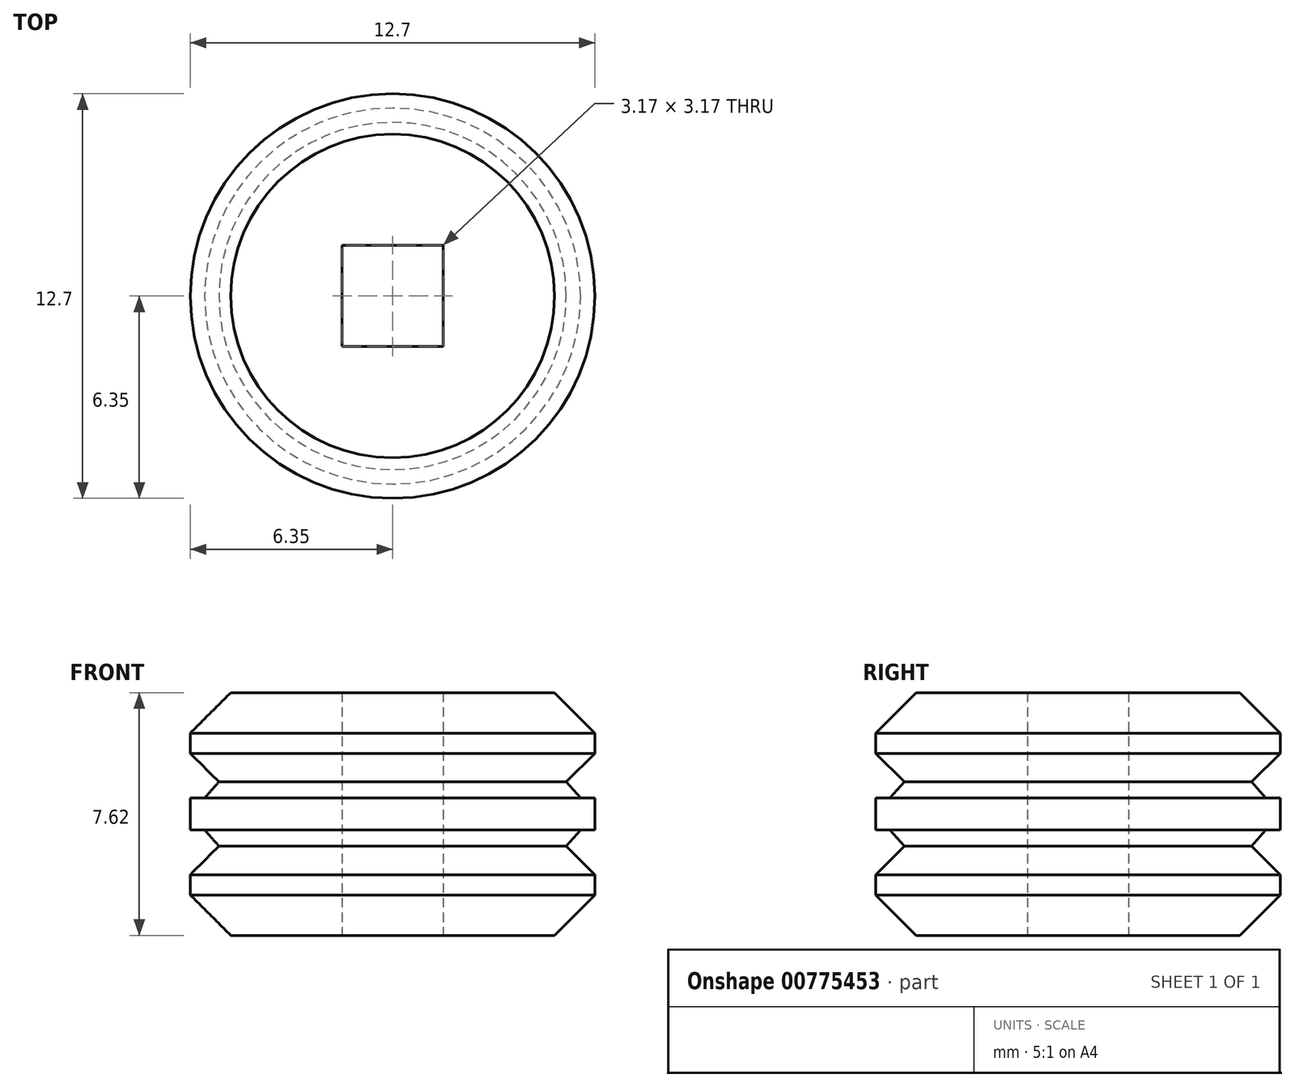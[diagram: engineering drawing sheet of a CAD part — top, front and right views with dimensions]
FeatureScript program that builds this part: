
annotation { "Feature Type Name" : "Feature", "Feature Type Description" : "" }
export const myFeature = defineFeature(function(context is Context, id is Id, definition is map)
    precondition{}
    {
        {
            var Q0;
            Q0=qCreatedBy(makeId("Front.planeOp"),FACE);
            var sketch = newSketch(context, id + "F0", { "sketchPlane" : qUnion([Q0])});
            skLineSegment(sketch, "E0.bottom", {"start": v(0, 0) * mm, "end": v(-6.35, 0) * mm});
            skLineSegment(sketch, "E0.top", {"start": v(0, 7.62) * mm, "end": v(-6.35, 7.62) * mm});
            skLineSegment(sketch, "E0.left", {"start": v(0, 0) * mm, "end": v(0, 7.62) * mm});
            skLineSegment(sketch, "E1", {"start": v(-6.35, 1.9) * mm, "end": v(-5.45, 2.8) * mm});
            skLineSegment(sketch, "E2.MirrorCS", {"start": v(-6.35, 5.72) * mm, "end": v(-5.45, 4.82) * mm});
            skLineSegment(sketch, "E3", {"start": v(-5.9, 3.3) * mm, "end": v(-6.35, 3.3) * mm});
            skLineSegment(sketch, "E4", {"start": v(-5.9, 3.3) * mm, "end": v(-5.45, 2.8) * mm});
            skLineSegment(sketch, "E5", {"start": v(-5.9, 4.31) * mm, "end": v(-6.35, 4.31) * mm});
            skLineSegment(sketch, "E6", {"start": v(-5.9, 4.31) * mm, "end": v(-5.45, 4.82) * mm});
            skLineSegment(sketch, "E7", {"start": v(-6.35, 3.3) * mm, "end": v(-6.35, 4.31) * mm});
            skLineSegment(sketch, "E8", {"start": v(-6.35, 1.9) * mm, "end": v(-6.35, 0) * mm});
            skLineSegment(sketch, "E9", {"start": v(-6.35, 5.72) * mm, "end": v(-6.35, 7.62) * mm});
            skSolve(sketch);
        }
        {
            var Q0;
            Q0=makeQuery(id+"F0.imprint","IMPRINT",FACE,{"disambiguationData":[TD([[makeQuery(id+"F0.imprint","IMPRINT",EDGE,{"derivedFrom":sQuery(id+"F0.wireOp",EDGE,"E0.bottom")}),-1.0]])]});
            var Q1;
            Q1=sQuery(id+"F0.wireOp",EDGE,"E0.left");
            revolve(context, id + "F1", {"surfaceOperationType" : NewSurfaceOperationType.NEW, "entities" : qUnion([Q0]), "axis" : qUnion([Q1]), "revolveType" : RevolveType.FULL});
        }
        {
            var Q0;
            Q0=makeQuery(id+"F1.opRevolve","SWEPT_EDGE",EDGE,{"disambiguationData":[OSD([sQuery(id+"F0.wireOp",EDGE,"E0.top"),sQuery(id+"F0.wireOp",EDGE,"E9")])]});
            var Q1;
            Q1=makeQuery(id+"F1.opRevolve","SWEPT_EDGE",EDGE,{"disambiguationData":[OSD([sQuery(id+"F0.wireOp",EDGE,"E0.bottom"),sQuery(id+"F0.wireOp",EDGE,"E8")])]});
            chamfer(context, id + "F2", {"entities" : qUnion([Q0, Q1]), "width" : 1.27 * mm, "tangentPropagation" : true});
        }
        {
            var Q0;
            Q0=makeQuery(id+"F1.opRevolve","SWEPT_FACE",FACE,{"disambiguationData":[OSD([sQuery(id+"F0.wireOp",EDGE,"E0.bottom")])]});
            var sketch = newSketch(context, id + "F3", { "sketchPlane" : qUnion([Q0])});
            skLineSegment(sketch, "E10.bottom", {"start": v(1.59, 1.59) * mm, "end": v(-1.59, 1.59) * mm});
            skLineSegment(sketch, "E10.top", {"start": v(1.59, -1.59) * mm, "end": v(-1.59, -1.59) * mm});
            skLineSegment(sketch, "E10.left", {"start": v(1.59, 1.59) * mm, "end": v(1.59, -1.59) * mm});
            skLineSegment(sketch, "E10.right", {"start": v(-1.59, 1.59) * mm, "end": v(-1.59, -1.59) * mm});
            skPoint(sketch, "E10.middle", {"position": v(0, 0) * mm});
            skSolve(sketch);
        }
        {
            var Q0;
            Q0=makeQuery(id+"F3.imprint","IMPRINT",FACE,{"disambiguationData":[TD([[makeQuery(id+"F3.imprint","IMPRINT",EDGE,{"derivedFrom":sQuery(id+"F3.wireOp",EDGE,"E10.bottom")}),1.0]])]});
            extrude(context, id + "F4", {"entities" : qUnion([Q0]), "operationType" : NewBodyOperationType.REMOVE, "oppositeDirection" : true, "depth" : 25.4 * mm, "offsetDistance" : 25.4 * mm});
        }
    });
